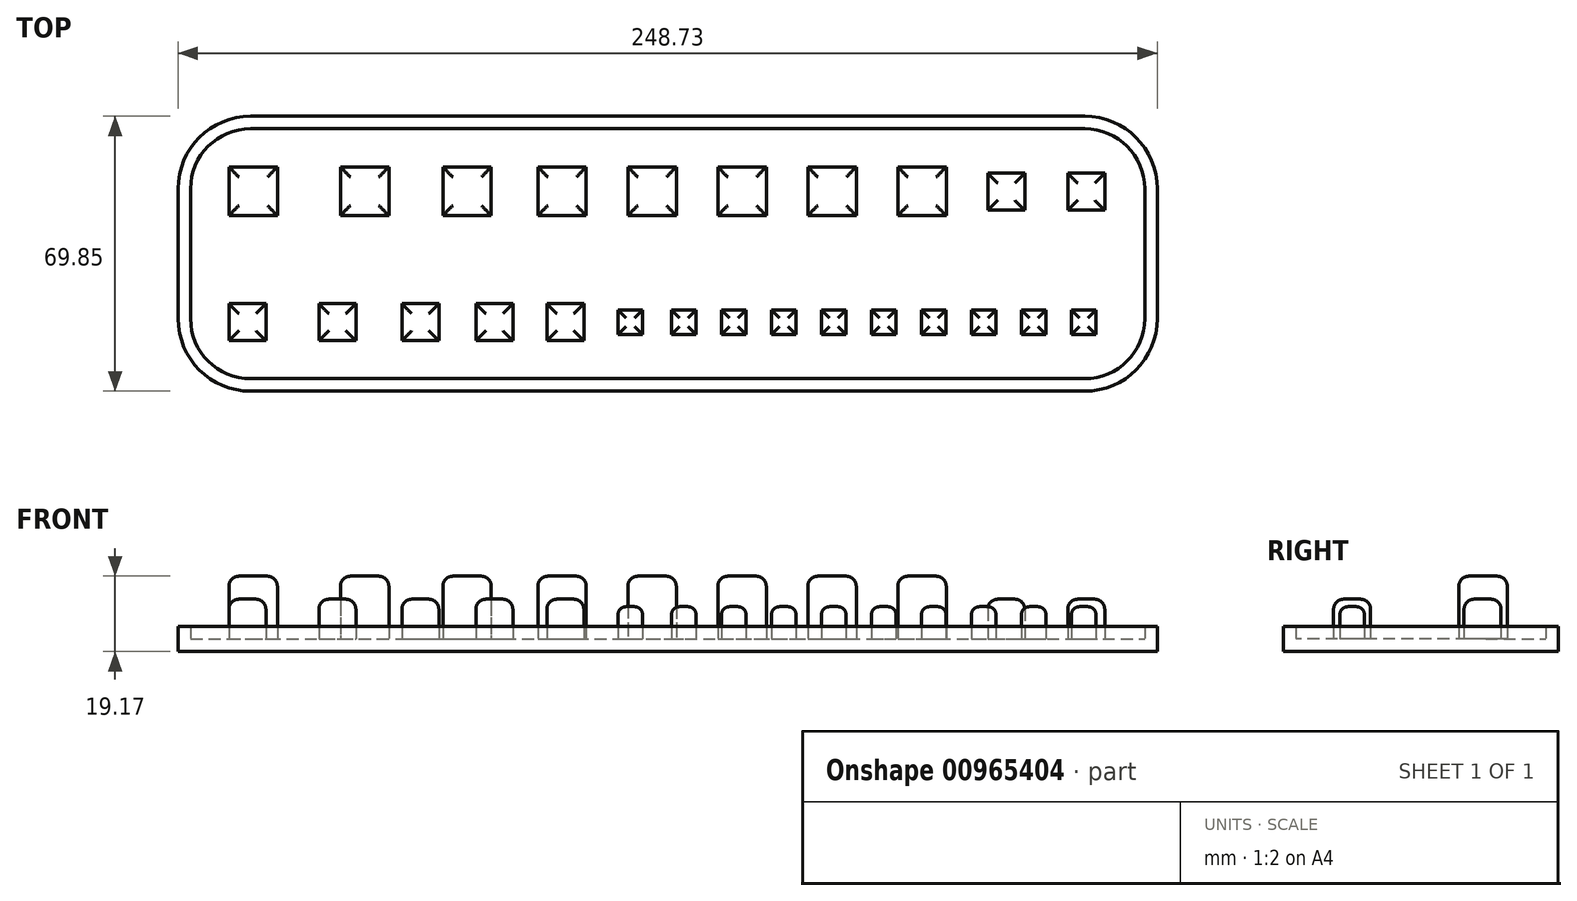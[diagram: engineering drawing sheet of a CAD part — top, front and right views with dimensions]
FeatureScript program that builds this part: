
annotation { "Feature Type Name" : "Feature", "Feature Type Description" : "" }
export const myFeature = defineFeature(function(context is Context, id is Id, definition is map)
    precondition{}
    {
        {
            var Q0;
            Q0=qCreatedBy(makeId("Top.planeOp"),FACE);
            var sketch = newSketch(context, id + "F0", { "sketchPlane" : qUnion([Q0])});
            skLineSegment(sketch, "E0.bottom", {"start": v(-9.72, 9.73) * mm, "end": v(232.66, 9.73) * mm});
            skLineSegment(sketch, "E0.top", {"start": v(-9.72, -53.77) * mm, "end": v(232.66, -53.77) * mm});
            skLineSegment(sketch, "E0.left", {"start": v(-9.72, 9.73) * mm, "end": v(-9.72, -53.77) * mm});
            skLineSegment(sketch, "E0.right", {"start": v(232.66, 9.73) * mm, "end": v(232.66, -53.77) * mm});
            skSolve(sketch);
        }
        {
            var Q0;
            Q0=makeQuery(id+"F0.imprint","IMPRINT",FACE,{"disambiguationData":[TD([[makeQuery(id+"F0.imprint","IMPRINT",EDGE,{"derivedFrom":sQuery(id+"F0.wireOp",EDGE,"E0.bottom")}),-1.0]])]});
            extrude(context, id + "F1", {"entities" : qUnion([Q0]), "oppositeDirection" : true, "depth" : 3.17 * mm, "offsetDistance" : 25.4 * mm});
        }
        {
            var Q0;
            Q0=qCreatedBy(makeId("Top.planeOp"),FACE);
            var sketch = newSketch(context, id + "F2", { "sketchPlane" : qUnion([Q0])});
            skLineSegment(sketch, "E1.bottom", {"start": v(0, 0) * mm, "end": v(12.32, 0) * mm});
            skLineSegment(sketch, "E1.top", {"start": v(0, -12.32) * mm, "end": v(12.32, -12.32) * mm});
            skLineSegment(sketch, "E1.left", {"start": v(0, 0) * mm, "end": v(0, -12.32) * mm});
            skLineSegment(sketch, "E1.right", {"start": v(12.32, 0) * mm, "end": v(12.32, -12.32) * mm});
            skLineSegment(sketch, "E2.1.0.0", {"start": v(28.32, 0) * mm, "end": v(40.64, 0) * mm});
            skLineSegment(sketch, "E2.1.0.1", {"start": v(28.32, -12.32) * mm, "end": v(40.64, -12.32) * mm});
            skLineSegment(sketch, "E2.1.0.2", {"start": v(40.64, 0) * mm, "end": v(40.64, -12.32) * mm});
            skLineSegment(sketch, "E2.1.0.3", {"start": v(28.32, 0) * mm, "end": v(28.32, -12.32) * mm});
            skLineSegment(sketch, "E2.direction1", {"start": v(0, -12.32) * mm, "end": v(28.32, -12.32) * mm, "construction": true});
            skLineSegment(sketch, "E3.1.0.0", {"start": v(54.36, 0) * mm, "end": v(54.36, -12.32) * mm});
            skLineSegment(sketch, "E3.1.0.1", {"start": v(54.36, 0) * mm, "end": v(66.67, 0) * mm});
            skLineSegment(sketch, "E3.1.0.2", {"start": v(54.36, -12.32) * mm, "end": v(66.67, -12.32) * mm});
            skLineSegment(sketch, "E3.1.0.3", {"start": v(66.67, 0) * mm, "end": v(66.67, -12.32) * mm});
            skLineSegment(sketch, "E3.1.0.4", {"start": v(26.04, -12.32) * mm, "end": v(54.36, -12.32) * mm, "construction": true});
            skLineSegment(sketch, "E3.direction1", {"start": v(0, -12.32) * mm, "end": v(26.04, -12.32) * mm, "construction": true});
            skLineSegment(sketch, "E4.1.0.0", {"start": v(78.49, 0) * mm, "end": v(78.49, -12.32) * mm});
            skLineSegment(sketch, "E4.1.0.1", {"start": v(50.16, -12.32) * mm, "end": v(78.49, -12.32) * mm, "construction": true});
            skLineSegment(sketch, "E4.1.0.2", {"start": v(90.8, 0) * mm, "end": v(90.8, -12.32) * mm});
            skLineSegment(sketch, "E4.1.0.3", {"start": v(78.49, -12.32) * mm, "end": v(90.8, -12.32) * mm});
            skLineSegment(sketch, "E4.1.0.4", {"start": v(78.49, 0) * mm, "end": v(90.8, 0) * mm});
            skLineSegment(sketch, "E4.direction1", {"start": v(26.04, -12.32) * mm, "end": v(50.16, -12.32) * mm, "construction": true});
            skLineSegment(sketch, "E5.1.0.0", {"start": v(101.35, 0) * mm, "end": v(101.35, -12.32) * mm});
            skLineSegment(sketch, "E5.1.0.1", {"start": v(113.67, 0) * mm, "end": v(113.67, -12.32) * mm});
            skLineSegment(sketch, "E5.1.0.2", {"start": v(101.35, 0) * mm, "end": v(113.67, 0) * mm});
            skLineSegment(sketch, "E5.1.0.3", {"start": v(101.35, -12.32) * mm, "end": v(113.67, -12.32) * mm});
            skLineSegment(sketch, "E5.1.0.4", {"start": v(73.03, -12.32) * mm, "end": v(101.35, -12.32) * mm, "construction": true});
            skLineSegment(sketch, "E5.direction1", {"start": v(50.16, -12.32) * mm, "end": v(73.03, -12.32) * mm, "construction": true});
            skLineSegment(sketch, "E6.1.0.0", {"start": v(124.2, 0) * mm, "end": v(136.53, 0) * mm});
            skLineSegment(sketch, "E6.1.0.1", {"start": v(124.2, 0) * mm, "end": v(124.2, -12.32) * mm});
            skLineSegment(sketch, "E6.1.0.2", {"start": v(136.53, 0) * mm, "end": v(136.53, -12.32) * mm});
            skLineSegment(sketch, "E6.1.0.3", {"start": v(124.2, -12.32) * mm, "end": v(136.53, -12.32) * mm});
            skLineSegment(sketch, "E6.1.0.4", {"start": v(95.89, -12.32) * mm, "end": v(124.2, -12.32) * mm, "construction": true});
            skLineSegment(sketch, "E6.direction1", {"start": v(72.14, -12.32) * mm, "end": v(95, -12.32) * mm, "construction": true});
            skLineSegment(sketch, "E7.1.0.0", {"start": v(147.07, 0) * mm, "end": v(159.38, 0) * mm});
            skLineSegment(sketch, "E7.1.0.1", {"start": v(159.38, 0) * mm, "end": v(159.38, -12.32) * mm});
            skLineSegment(sketch, "E7.1.0.2", {"start": v(147.07, 0) * mm, "end": v(147.07, -12.32) * mm});
            skLineSegment(sketch, "E7.1.0.3", {"start": v(147.07, -12.32) * mm, "end": v(159.38, -12.32) * mm});
            skLineSegment(sketch, "E7.1.0.4", {"start": v(118.75, -12.32) * mm, "end": v(147.07, -12.32) * mm, "construction": true});
            skLineSegment(sketch, "E7.direction1", {"start": v(95.89, -12.32) * mm, "end": v(118.75, -12.32) * mm, "construction": true});
            skLineSegment(sketch, "E8.1.0.0", {"start": v(141.6, -12.32) * mm, "end": v(169.93, -12.32) * mm, "construction": true});
            skLineSegment(sketch, "E8.1.0.1", {"start": v(169.93, 0) * mm, "end": v(169.93, -12.32) * mm});
            skLineSegment(sketch, "E8.1.0.2", {"start": v(169.93, -12.32) * mm, "end": v(182.25, -12.32) * mm});
            skLineSegment(sketch, "E8.1.0.3", {"start": v(169.93, 0) * mm, "end": v(182.25, 0) * mm});
            skLineSegment(sketch, "E8.1.0.4", {"start": v(182.25, 0) * mm, "end": v(182.25, -12.32) * mm});
            skLineSegment(sketch, "E8.direction1", {"start": v(118.75, -12.32) * mm, "end": v(141.6, -12.32) * mm, "construction": true});
            skSolve(sketch);
        }
        {
            var Q0;
            Q0=makeQuery(id+"F2.imprint","IMPRINT",FACE,{"disambiguationData":[TD([[makeQuery(id+"F2.imprint","IMPRINT",EDGE,{"derivedFrom":sQuery(id+"F2.wireOp",EDGE,"E1.bottom")}),-1.0]])]});
            var Q1;
            Q1=makeQuery(id+"F2.imprint","IMPRINT",FACE,{"disambiguationData":[TD([[makeQuery(id+"F2.imprint","IMPRINT",EDGE,{"derivedFrom":sQuery(id+"F2.wireOp",EDGE,"E2.1.0.0")}),-1.0]])]});
            var Q2;
            Q2=makeQuery(id+"F2.imprint","IMPRINT",FACE,{"disambiguationData":[TD([[makeQuery(id+"F2.imprint","IMPRINT",EDGE,{"derivedFrom":sQuery(id+"F2.wireOp",EDGE,"E3.1.0.0")}),1.0]])]});
            var Q3;
            Q3=makeQuery(id+"F2.imprint","IMPRINT",FACE,{"disambiguationData":[TD([[makeQuery(id+"F2.imprint","IMPRINT",EDGE,{"derivedFrom":sQuery(id+"F2.wireOp",EDGE,"E4.1.0.0")}),1.0]])]});
            var Q4;
            Q4=makeQuery(id+"F2.imprint","IMPRINT",FACE,{"disambiguationData":[TD([[makeQuery(id+"F2.imprint","IMPRINT",EDGE,{"derivedFrom":sQuery(id+"F2.wireOp",EDGE,"E5.1.0.0")}),1.0]])]});
            var Q5;
            Q5=makeQuery(id+"F2.imprint","IMPRINT",FACE,{"disambiguationData":[TD([[makeQuery(id+"F2.imprint","IMPRINT",EDGE,{"derivedFrom":sQuery(id+"F2.wireOp",EDGE,"E6.1.0.0")}),-1.0]])]});
            var Q6;
            Q6=makeQuery(id+"F2.imprint","IMPRINT",FACE,{"disambiguationData":[TD([[makeQuery(id+"F2.imprint","IMPRINT",EDGE,{"derivedFrom":sQuery(id+"F2.wireOp",EDGE,"E7.1.0.0")}),-1.0]])]});
            var Q7;
            Q7=makeQuery(id+"F2.imprint","IMPRINT",FACE,{"disambiguationData":[TD([[makeQuery(id+"F2.imprint","IMPRINT",EDGE,{"derivedFrom":sQuery(id+"F2.wireOp",EDGE,"E8.1.0.1")}),1.0]])]});
            extrude(context, id + "F3", {"entities" : qUnion([Q0, Q1, Q2, Q3, Q4, Q5, Q6, Q7]), "operationType" : NewBodyOperationType.ADD, "depth" : 16 * mm, "offsetDistance" : 25.4 * mm});
        }
        {
            var Q0;
            Q0=makeQuery(id+"F1.opExtrude","CAP_FACE",FACE,{"disambiguationData":[OSD([sQuery(id+"F0.wireOp",EDGE,"E0.bottom"),sQuery(id+"F0.wireOp",EDGE,"E0.top"),sQuery(id+"F0.wireOp",EDGE,"E0.left"),sQuery(id+"F0.wireOp",EDGE,"E0.right")])],"isStart":true});
            var sketch = newSketch(context, id + "F4", { "sketchPlane" : qUnion([Q0])});
            skLineSegment(sketch, "E9", {"start": v(0, -34.73) * mm, "end": v(193.08, -34.73) * mm, "construction": true});
            skLineSegment(sketch, "E10.bottom", {"start": v(0, -34.73) * mm, "end": v(9.4, -34.73) * mm});
            skLineSegment(sketch, "E10.top", {"start": v(0, -44.13) * mm, "end": v(9.4, -44.13) * mm});
            skLineSegment(sketch, "E10.left", {"start": v(0, -34.73) * mm, "end": v(0, -44.13) * mm});
            skLineSegment(sketch, "E10.right", {"start": v(9.4, -34.73) * mm, "end": v(9.4, -44.13) * mm});
            skLineSegment(sketch, "E11.bottom", {"start": v(22.86, -34.73) * mm, "end": v(32.26, -34.73) * mm});
            skLineSegment(sketch, "E11.top", {"start": v(22.86, -44.13) * mm, "end": v(32.26, -44.13) * mm});
            skLineSegment(sketch, "E11.left", {"start": v(22.86, -34.73) * mm, "end": v(22.86, -44.13) * mm});
            skLineSegment(sketch, "E11.right", {"start": v(32.26, -34.73) * mm, "end": v(32.26, -44.13) * mm});
            skLineSegment(sketch, "E12.bottom", {"start": v(43.94, -34.73) * mm, "end": v(53.34, -34.73) * mm});
            skLineSegment(sketch, "E12.top", {"start": v(43.94, -44.13) * mm, "end": v(53.34, -44.13) * mm});
            skLineSegment(sketch, "E12.left", {"start": v(43.94, -34.73) * mm, "end": v(43.94, -44.13) * mm});
            skLineSegment(sketch, "E12.right", {"start": v(53.34, -34.73) * mm, "end": v(53.34, -44.13) * mm});
            skLineSegment(sketch, "E13.bottom", {"start": v(62.74, -34.73) * mm, "end": v(72.14, -34.73) * mm});
            skLineSegment(sketch, "E13.top", {"start": v(62.74, -44.13) * mm, "end": v(72.14, -44.13) * mm});
            skLineSegment(sketch, "E13.left", {"start": v(62.74, -34.73) * mm, "end": v(62.74, -44.13) * mm});
            skLineSegment(sketch, "E13.right", {"start": v(72.14, -34.73) * mm, "end": v(72.14, -44.13) * mm});
            skLineSegment(sketch, "E14.bottom", {"start": v(80.77, -34.73) * mm, "end": v(90.17, -34.73) * mm});
            skLineSegment(sketch, "E14.top", {"start": v(80.77, -44.13) * mm, "end": v(90.17, -44.13) * mm});
            skLineSegment(sketch, "E14.left", {"start": v(80.77, -34.73) * mm, "end": v(80.77, -44.13) * mm});
            skLineSegment(sketch, "E14.right", {"start": v(90.17, -34.73) * mm, "end": v(90.17, -44.13) * mm});
            skLineSegment(sketch, "E15.bottom", {"start": v(192.79, -1.59) * mm, "end": v(202.18, -1.59) * mm});
            skLineSegment(sketch, "E15.top", {"start": v(192.79, -10.99) * mm, "end": v(202.18, -10.99) * mm});
            skLineSegment(sketch, "E15.left", {"start": v(192.79, -1.59) * mm, "end": v(192.79, -10.99) * mm});
            skLineSegment(sketch, "E15.right", {"start": v(202.18, -1.59) * mm, "end": v(202.18, -10.99) * mm});
            skLineSegment(sketch, "E16.1.0.0", {"start": v(213.1, -1.59) * mm, "end": v(222.5, -1.59) * mm});
            skLineSegment(sketch, "E16.1.0.1", {"start": v(213.1, -10.99) * mm, "end": v(222.5, -10.99) * mm});
            skLineSegment(sketch, "E16.1.0.2", {"start": v(222.5, -1.59) * mm, "end": v(222.5, -10.99) * mm});
            skLineSegment(sketch, "E16.1.0.3", {"start": v(213.1, -1.59) * mm, "end": v(213.1, -10.99) * mm});
            skLineSegment(sketch, "E16.direction1", {"start": v(192.79, -10.99) * mm, "end": v(213.1, -10.99) * mm, "construction": true});
            skSolve(sketch);
        }
        {
            var Q0;
            Q0=makeQuery(id+"F4.imprint","IMPRINT",FACE,{"disambiguationData":[TD([[makeQuery(id+"F4.imprint","IMPRINT",EDGE,{"derivedFrom":sQuery(id+"F4.wireOp",EDGE,"E12.bottom")}),-1.0]])]});
            var Q1;
            Q1=makeQuery(id+"F4.imprint","IMPRINT",FACE,{"disambiguationData":[TD([[makeQuery(id+"F4.imprint","IMPRINT",EDGE,{"derivedFrom":sQuery(id+"F4.wireOp",EDGE,"E13.bottom")}),-1.0]])]});
            var Q2;
            Q2=makeQuery(id+"F4.imprint","IMPRINT",FACE,{"disambiguationData":[TD([[makeQuery(id+"F4.imprint","IMPRINT",EDGE,{"derivedFrom":sQuery(id+"F4.wireOp",EDGE,"E14.bottom")}),-1.0]])]});
            var Q3;
            Q3=makeQuery(id+"F4.imprint","IMPRINT",FACE,{"disambiguationData":[TD([[makeQuery(id+"F4.imprint","IMPRINT",EDGE,{"derivedFrom":sQuery(id+"F4.wireOp",EDGE,"HuPphu0x-Gtiq-LhBo-5UTa-TvdvrvVJAFvw.bottom")}),-1.0]])]});
            var Q4;
            Q4=makeQuery(id+"F4.imprint","IMPRINT",FACE,{"disambiguationData":[TD([[makeQuery(id+"F4.imprint","IMPRINT",EDGE,{"derivedFrom":sQuery(id+"F4.wireOp",EDGE,"E11.bottom")}),-1.0]])]});
            var Q5;
            Q5=makeQuery(id+"F4.imprint","IMPRINT",FACE,{"disambiguationData":[TD([[makeQuery(id+"F4.imprint","IMPRINT",EDGE,{"derivedFrom":sQuery(id+"F4.wireOp",EDGE,"E10.bottom")}),-1.0]])]});
            var Q6;
            Q6=makeQuery(id+"F4.imprint","IMPRINT",FACE,{"disambiguationData":[TD([[makeQuery(id+"F4.imprint","IMPRINT",EDGE,{"derivedFrom":sQuery(id+"F4.wireOp",EDGE,"E15.bottom")}),-1.0]])]});
            var Q7;
            Q7=makeQuery(id+"F4.imprint","IMPRINT",FACE,{"disambiguationData":[TD([[makeQuery(id+"F4.imprint","IMPRINT",EDGE,{"derivedFrom":sQuery(id+"F4.wireOp",EDGE,"E16.1.0.0")}),-1.0]])]});
            extrude(context, id + "F5", {"entities" : qUnion([Q0, Q1, Q2, Q3, Q4, Q5, Q6, Q7]), "operationType" : NewBodyOperationType.ADD, "depth" : 10.16 * mm, "offsetDistance" : 25.4 * mm});
        }
        {
            var Q0;
            Q0=makeQuery(id+"F1.opExtrude","SWEPT_EDGE",EDGE,{"disambiguationData":[OSD([sQuery(id+"F0.wireOp",EDGE,"E0.bottom"),sQuery(id+"F0.wireOp",EDGE,"E0.left")])]});
            var Q1;
            Q1=makeQuery(id+"F1.opExtrude","SWEPT_EDGE",EDGE,{"disambiguationData":[OSD([sQuery(id+"F0.wireOp",EDGE,"E0.bottom"),sQuery(id+"F0.wireOp",EDGE,"E0.right")])]});
            var Q2;
            Q2=makeQuery(id+"F1.opExtrude","SWEPT_EDGE",EDGE,{"disambiguationData":[OSD([sQuery(id+"F0.wireOp",EDGE,"E0.top"),sQuery(id+"F0.wireOp",EDGE,"E0.right")])]});
            var Q3;
            Q3=makeQuery(id+"F1.opExtrude","SWEPT_EDGE",EDGE,{"disambiguationData":[OSD([sQuery(id+"F0.wireOp",EDGE,"E0.top"),sQuery(id+"F0.wireOp",EDGE,"E0.left")])]});
            fillet(context, id + "F6", {"entities" : qUnion([Q0, Q1, Q2, Q3]), "radius" : 15.24 * mm, "tangentPropagation" : true, "allowEdgeOverflow" : false});
        }
        {
            var Q0;
            Q0=makeQuery(id+"F3.opExtrude","CAP_FACE",FACE,{"disambiguationData":[OSD([sQuery(id+"F2.wireOp",EDGE,"E1.bottom"),sQuery(id+"F2.wireOp",EDGE,"E1.top"),sQuery(id+"F2.wireOp",EDGE,"E1.left"),sQuery(id+"F2.wireOp",EDGE,"E1.right")])],"isStart":false});
            var Q1;
            Q1=makeQuery(id+"F3.opExtrude","CAP_FACE",FACE,{"disambiguationData":[OSD([sQuery(id+"F2.wireOp",EDGE,"E2.1.0.0"),sQuery(id+"F2.wireOp",EDGE,"E2.1.0.1"),sQuery(id+"F2.wireOp",EDGE,"E2.1.0.2"),sQuery(id+"F2.wireOp",EDGE,"E2.1.0.3")])],"isStart":false});
            var Q2;
            Q2=makeQuery(id+"F3.opExtrude","CAP_FACE",FACE,{"disambiguationData":[OSD([sQuery(id+"F2.wireOp",EDGE,"E3.1.0.0"),sQuery(id+"F2.wireOp",EDGE,"E3.1.0.1"),sQuery(id+"F2.wireOp",EDGE,"E3.1.0.2"),sQuery(id+"F2.wireOp",EDGE,"E3.1.0.3")])],"isStart":false});
            var Q3;
            Q3=makeQuery(id+"F3.opExtrude","CAP_FACE",FACE,{"disambiguationData":[OSD([sQuery(id+"F2.wireOp",EDGE,"E4.1.0.0"),sQuery(id+"F2.wireOp",EDGE,"E4.1.0.2"),sQuery(id+"F2.wireOp",EDGE,"E4.1.0.3"),sQuery(id+"F2.wireOp",EDGE,"E4.1.0.4")])],"isStart":false});
            var Q4;
            Q4=makeQuery(id+"F3.opExtrude","CAP_FACE",FACE,{"disambiguationData":[OSD([sQuery(id+"F2.wireOp",EDGE,"E5.1.0.0"),sQuery(id+"F2.wireOp",EDGE,"E5.1.0.1"),sQuery(id+"F2.wireOp",EDGE,"E5.1.0.2"),sQuery(id+"F2.wireOp",EDGE,"E5.1.0.3")])],"isStart":false});
            var Q5;
            Q5=makeQuery(id+"F3.opExtrude","CAP_FACE",FACE,{"disambiguationData":[OSD([sQuery(id+"F2.wireOp",EDGE,"E6.1.0.0"),sQuery(id+"F2.wireOp",EDGE,"E6.1.0.1"),sQuery(id+"F2.wireOp",EDGE,"E6.1.0.2"),sQuery(id+"F2.wireOp",EDGE,"E6.1.0.3")])],"isStart":false});
            var Q6;
            Q6=makeQuery(id+"F3.opExtrude","CAP_FACE",FACE,{"disambiguationData":[OSD([sQuery(id+"F2.wireOp",EDGE,"E7.1.0.0"),sQuery(id+"F2.wireOp",EDGE,"E7.1.0.1"),sQuery(id+"F2.wireOp",EDGE,"E7.1.0.2"),sQuery(id+"F2.wireOp",EDGE,"E7.1.0.3")])],"isStart":false});
            var Q7;
            Q7=makeQuery(id+"F3.opExtrude","CAP_FACE",FACE,{"disambiguationData":[OSD([sQuery(id+"F2.wireOp",EDGE,"E8.1.0.1"),sQuery(id+"F2.wireOp",EDGE,"E8.1.0.2"),sQuery(id+"F2.wireOp",EDGE,"E8.1.0.3"),sQuery(id+"F2.wireOp",EDGE,"E8.1.0.4")])],"isStart":false});
            fillet(context, id + "F7", {"entities" : qUnion([Q0, Q1, Q2, Q3, Q4, Q5, Q6, Q7]), "radius" : 2.54 * mm, "tangentPropagation" : true, "allowEdgeOverflow" : false});
        }
        {
            var Q0;
            Q0=makeQuery(id+"F5.opExtrude","CAP_FACE",FACE,{"disambiguationData":[OSD([sQuery(id+"F4.wireOp",EDGE,"E10.bottom"),sQuery(id+"F4.wireOp",EDGE,"E10.top"),sQuery(id+"F4.wireOp",EDGE,"E10.left"),sQuery(id+"F4.wireOp",EDGE,"E10.right")])],"isStart":false});
            var Q1;
            Q1=makeQuery(id+"F5.opExtrude","CAP_FACE",FACE,{"disambiguationData":[OSD([sQuery(id+"F4.wireOp",EDGE,"E11.bottom"),sQuery(id+"F4.wireOp",EDGE,"E11.top"),sQuery(id+"F4.wireOp",EDGE,"E11.left"),sQuery(id+"F4.wireOp",EDGE,"E11.right")])],"isStart":false});
            var Q2;
            Q2=makeQuery(id+"F5.opExtrude","CAP_FACE",FACE,{"disambiguationData":[OSD([sQuery(id+"F4.wireOp",EDGE,"E12.bottom"),sQuery(id+"F4.wireOp",EDGE,"E12.top"),sQuery(id+"F4.wireOp",EDGE,"E12.left"),sQuery(id+"F4.wireOp",EDGE,"E12.right")])],"isStart":false});
            var Q3;
            Q3=makeQuery(id+"F5.opExtrude","CAP_FACE",FACE,{"disambiguationData":[OSD([sQuery(id+"F4.wireOp",EDGE,"E13.bottom"),sQuery(id+"F4.wireOp",EDGE,"E13.top"),sQuery(id+"F4.wireOp",EDGE,"E13.left"),sQuery(id+"F4.wireOp",EDGE,"E13.right")])],"isStart":false});
            var Q4;
            Q4=makeQuery(id+"F5.opExtrude","CAP_FACE",FACE,{"disambiguationData":[OSD([sQuery(id+"F4.wireOp",EDGE,"E14.bottom"),sQuery(id+"F4.wireOp",EDGE,"E14.top"),sQuery(id+"F4.wireOp",EDGE,"E14.left"),sQuery(id+"F4.wireOp",EDGE,"E14.right")])],"isStart":false});
            var Q5;
            Q5=makeQuery(id+"F5.opExtrude","CAP_FACE",FACE,{"disambiguationData":[OSD([sQuery(id+"F4.wireOp",EDGE,"HuPphu0x-Gtiq-LhBo-5UTa-TvdvrvVJAFvw.bottom"),sQuery(id+"F4.wireOp",EDGE,"HuPphu0x-Gtiq-LhBo-5UTa-TvdvrvVJAFvw.top"),sQuery(id+"F4.wireOp",EDGE,"HuPphu0x-Gtiq-LhBo-5UTa-TvdvrvVJAFvw.left"),sQuery(id+"F4.wireOp",EDGE,"HuPphu0x-Gtiq-LhBo-5UTa-TvdvrvVJAFvw.right")])],"isStart":false});
            var Q6;
            Q6=makeQuery(id+"F5.opExtrude","CAP_FACE",FACE,{"disambiguationData":[OSD([sQuery(id+"F4.wireOp",EDGE,"E15.bottom"),sQuery(id+"F4.wireOp",EDGE,"E15.top"),sQuery(id+"F4.wireOp",EDGE,"E15.left"),sQuery(id+"F4.wireOp",EDGE,"E15.right")])],"isStart":false});
            var Q7;
            Q7=makeQuery(id+"F5.opExtrude","CAP_FACE",FACE,{"disambiguationData":[OSD([sQuery(id+"F4.wireOp",EDGE,"E16.1.0.0"),sQuery(id+"F4.wireOp",EDGE,"E16.1.0.1"),sQuery(id+"F4.wireOp",EDGE,"E16.1.0.2"),sQuery(id+"F4.wireOp",EDGE,"E16.1.0.3")])],"isStart":false});
            fillet(context, id + "F8", {"entities" : qUnion([Q0, Q1, Q2, Q3, Q4, Q5, Q6, Q7]), "radius" : 2.54 * mm, "tangentPropagation" : true, "allowEdgeOverflow" : false});
        }
        {
            var Q0;
            Q0=makeQuery(id+"F1.opExtrude","CAP_FACE",FACE,{"disambiguationData":[OSD([sQuery(id+"F0.wireOp",EDGE,"E0.bottom"),sQuery(id+"F0.wireOp",EDGE,"E0.top"),sQuery(id+"F0.wireOp",EDGE,"E0.left"),sQuery(id+"F0.wireOp",EDGE,"E0.right")])],"isStart":true});
            var sketch = newSketch(context, id + "F9", { "sketchPlane" : qUnion([Q0])});
            skLineSegment(sketch, "E17", {"start": v(113.95, -36.32) * mm, "end": v(235.74, -36.32) * mm, "construction": true});
            skLineSegment(sketch, "E18.bottom", {"start": v(98.87, -36.32) * mm, "end": v(105.1, -36.32) * mm});
            skLineSegment(sketch, "E18.top", {"start": v(98.87, -42.55) * mm, "end": v(105.1, -42.55) * mm});
            skLineSegment(sketch, "E18.left", {"start": v(98.87, -36.32) * mm, "end": v(98.87, -42.55) * mm});
            skLineSegment(sketch, "E18.right", {"start": v(105.1, -36.32) * mm, "end": v(105.1, -42.55) * mm});
            skPoint(sketch, "E19.oppositeSnap0", {"position": v(101.98, -42.55) * mm});
            skLineSegment(sketch, "E19.bottom", {"start": v(112.46, -36.32) * mm, "end": v(118.68, -36.32) * mm});
            skLineSegment(sketch, "E19.top", {"start": v(112.46, -42.55) * mm, "end": v(118.68, -42.55) * mm});
            skLineSegment(sketch, "E19.left", {"start": v(112.46, -36.32) * mm, "end": v(112.46, -42.54) * mm});
            skLineSegment(sketch, "E19.right", {"start": v(118.68, -36.32) * mm, "end": v(118.68, -42.54) * mm});
            skLineSegment(sketch, "E20.1.0.0", {"start": v(125.16, -36.32) * mm, "end": v(125.16, -42.54) * mm});
            skLineSegment(sketch, "E20.1.0.1", {"start": v(125.16, -42.55) * mm, "end": v(131.38, -42.55) * mm});
            skLineSegment(sketch, "E20.1.0.2", {"start": v(131.38, -36.32) * mm, "end": v(131.38, -42.54) * mm});
            skLineSegment(sketch, "E20.1.0.3", {"start": v(125.16, -36.32) * mm, "end": v(131.38, -36.32) * mm});
            skLineSegment(sketch, "E20.2.0.0", {"start": v(137.86, -36.32) * mm, "end": v(137.86, -42.54) * mm});
            skLineSegment(sketch, "E20.2.0.1", {"start": v(137.86, -42.55) * mm, "end": v(144.08, -42.55) * mm});
            skLineSegment(sketch, "E20.2.0.2", {"start": v(144.08, -36.32) * mm, "end": v(144.08, -42.54) * mm});
            skLineSegment(sketch, "E20.2.0.3", {"start": v(137.86, -36.32) * mm, "end": v(144.08, -36.32) * mm});
            skLineSegment(sketch, "E20.3.0.0", {"start": v(150.56, -36.32) * mm, "end": v(150.56, -42.54) * mm});
            skLineSegment(sketch, "E20.3.0.1", {"start": v(150.56, -42.55) * mm, "end": v(156.78, -42.55) * mm});
            skLineSegment(sketch, "E20.3.0.2", {"start": v(156.78, -36.32) * mm, "end": v(156.78, -42.54) * mm});
            skLineSegment(sketch, "E20.3.0.3", {"start": v(150.56, -36.32) * mm, "end": v(156.78, -36.32) * mm});
            skLineSegment(sketch, "E20.4.0.0", {"start": v(163.26, -36.32) * mm, "end": v(163.26, -42.54) * mm});
            skLineSegment(sketch, "E20.4.0.1", {"start": v(163.26, -42.55) * mm, "end": v(169.48, -42.55) * mm});
            skLineSegment(sketch, "E20.4.0.2", {"start": v(169.48, -36.32) * mm, "end": v(169.48, -42.54) * mm});
            skLineSegment(sketch, "E20.4.0.3", {"start": v(163.26, -36.32) * mm, "end": v(169.48, -36.32) * mm});
            skLineSegment(sketch, "E20.5.0.0", {"start": v(175.96, -36.32) * mm, "end": v(175.96, -42.54) * mm});
            skLineSegment(sketch, "E20.5.0.1", {"start": v(175.96, -42.55) * mm, "end": v(182.18, -42.55) * mm});
            skLineSegment(sketch, "E20.5.0.2", {"start": v(182.18, -36.32) * mm, "end": v(182.18, -42.54) * mm});
            skLineSegment(sketch, "E20.5.0.3", {"start": v(175.96, -36.32) * mm, "end": v(182.18, -36.32) * mm});
            skLineSegment(sketch, "E20.6.0.0", {"start": v(188.66, -36.32) * mm, "end": v(188.66, -42.54) * mm});
            skLineSegment(sketch, "E20.6.0.1", {"start": v(188.66, -42.55) * mm, "end": v(194.88, -42.55) * mm});
            skLineSegment(sketch, "E20.6.0.2", {"start": v(194.88, -36.32) * mm, "end": v(194.88, -42.54) * mm});
            skLineSegment(sketch, "E20.6.0.3", {"start": v(188.66, -36.32) * mm, "end": v(194.88, -36.32) * mm});
            skLineSegment(sketch, "E20.7.0.0", {"start": v(201.36, -36.32) * mm, "end": v(201.36, -42.54) * mm});
            skLineSegment(sketch, "E20.7.0.1", {"start": v(201.36, -42.55) * mm, "end": v(207.58, -42.55) * mm});
            skLineSegment(sketch, "E20.7.0.2", {"start": v(207.58, -36.32) * mm, "end": v(207.58, -42.54) * mm});
            skLineSegment(sketch, "E20.7.0.3", {"start": v(201.36, -36.32) * mm, "end": v(207.58, -36.32) * mm});
            skLineSegment(sketch, "E20.8.0.0", {"start": v(214.06, -36.32) * mm, "end": v(214.06, -42.54) * mm});
            skLineSegment(sketch, "E20.8.0.1", {"start": v(214.06, -42.55) * mm, "end": v(220.28, -42.55) * mm});
            skLineSegment(sketch, "E20.8.0.2", {"start": v(220.28, -36.32) * mm, "end": v(220.28, -42.54) * mm});
            skLineSegment(sketch, "E20.8.0.3", {"start": v(214.06, -36.32) * mm, "end": v(220.28, -36.32) * mm});
            skLineSegment(sketch, "E20.direction1", {"start": v(112.46, -42.55) * mm, "end": v(125.16, -42.55) * mm, "construction": true});
            skSolve(sketch);
        }
        {
            var Q0;
            Q0=makeQuery(id+"F9.imprint","IMPRINT",FACE,{"disambiguationData":[TD([[makeQuery(id+"F9.imprint","IMPRINT",EDGE,{"derivedFrom":sQuery(id+"F9.wireOp",EDGE,"E18.bottom")}),-1.0]])]});
            var Q1;
            Q1=makeQuery(id+"F9.imprint","IMPRINT",FACE,{"disambiguationData":[TD([[makeQuery(id+"F9.imprint","IMPRINT",EDGE,{"derivedFrom":sQuery(id+"F9.wireOp",EDGE,"E19.bottom")}),-1.0]])]});
            var Q2;
            Q2=makeQuery(id+"F9.imprint","IMPRINT",FACE,{"disambiguationData":[TD([[makeQuery(id+"F9.imprint","IMPRINT",EDGE,{"derivedFrom":sQuery(id+"F9.wireOp",EDGE,"E20.1.0.0")}),1.0]])]});
            var Q3;
            Q3=makeQuery(id+"F9.imprint","IMPRINT",FACE,{"disambiguationData":[TD([[makeQuery(id+"F9.imprint","IMPRINT",EDGE,{"derivedFrom":sQuery(id+"F9.wireOp",EDGE,"E20.2.0.0")}),1.0]])]});
            var Q4;
            Q4=makeQuery(id+"F9.imprint","IMPRINT",FACE,{"disambiguationData":[TD([[makeQuery(id+"F9.imprint","IMPRINT",EDGE,{"derivedFrom":sQuery(id+"F9.wireOp",EDGE,"E20.3.0.0")}),1.0]])]});
            var Q5;
            Q5=makeQuery(id+"F9.imprint","IMPRINT",FACE,{"disambiguationData":[TD([[makeQuery(id+"F9.imprint","IMPRINT",EDGE,{"derivedFrom":sQuery(id+"F9.wireOp",EDGE,"E20.4.0.0")}),1.0]])]});
            var Q6;
            Q6=makeQuery(id+"F9.imprint","IMPRINT",FACE,{"disambiguationData":[TD([[makeQuery(id+"F9.imprint","IMPRINT",EDGE,{"derivedFrom":sQuery(id+"F9.wireOp",EDGE,"E20.5.0.0")}),1.0]])]});
            var Q7;
            Q7=makeQuery(id+"F9.imprint","IMPRINT",FACE,{"disambiguationData":[TD([[makeQuery(id+"F9.imprint","IMPRINT",EDGE,{"derivedFrom":sQuery(id+"F9.wireOp",EDGE,"E20.6.0.0")}),1.0]])]});
            var Q8;
            Q8=makeQuery(id+"F9.imprint","IMPRINT",FACE,{"disambiguationData":[TD([[makeQuery(id+"F9.imprint","IMPRINT",EDGE,{"derivedFrom":sQuery(id+"F9.wireOp",EDGE,"E20.7.0.0")}),1.0]])]});
            var Q9;
            Q9=makeQuery(id+"F9.imprint","IMPRINT",FACE,{"disambiguationData":[TD([[makeQuery(id+"F9.imprint","IMPRINT",EDGE,{"derivedFrom":sQuery(id+"F9.wireOp",EDGE,"E20.8.0.0")}),1.0]])]});
            var Q10;
            Q10=sQuery(id+"F9.wireOp",EDGE,"E18.left");
            var Q11;
            Q11=sQuery(id+"F9.wireOp",EDGE,"E18.bottom");
            var Q12;
            Q12=sQuery(id+"F9.wireOp",EDGE,"E18.right");
            var Q13;
            Q13=sQuery(id+"F9.wireOp",EDGE,"E18.top");
            extrude(context, id + "F10", {"entities" : qUnion([Q0, Q1, Q2, Q3, Q4, Q5, Q6, Q7, Q8, Q9]), "operationType" : NewBodyOperationType.ADD, "surfaceEntities" : qUnion([Q10, Q11, Q12, Q13]), "depth" : 8.25 * mm, "offsetDistance" : 25.4 * mm});
        }
        {
            var Q0;
            Q0=makeQuery(id+"F10.opExtrude","CAP_FACE",FACE,{"disambiguationData":[OSD([sQuery(id+"F9.wireOp",EDGE,"E18.bottom"),sQuery(id+"F9.wireOp",EDGE,"E18.top"),sQuery(id+"F9.wireOp",EDGE,"E18.left"),sQuery(id+"F9.wireOp",EDGE,"E18.right")])],"isStart":false});
            var Q1;
            Q1=makeQuery(id+"F10.opExtrude","CAP_FACE",FACE,{"disambiguationData":[OSD([sQuery(id+"F9.wireOp",EDGE,"E19.bottom"),sQuery(id+"F9.wireOp",EDGE,"E19.top"),sQuery(id+"F9.wireOp",EDGE,"E19.left"),sQuery(id+"F9.wireOp",EDGE,"E19.right")])],"isStart":false});
            var Q2;
            Q2=makeQuery(id+"F10.opExtrude","CAP_FACE",FACE,{"disambiguationData":[OSD([sQuery(id+"F9.wireOp",EDGE,"E20.1.0.0"),sQuery(id+"F9.wireOp",EDGE,"E20.1.0.1"),sQuery(id+"F9.wireOp",EDGE,"E20.1.0.2"),sQuery(id+"F9.wireOp",EDGE,"E20.1.0.3")])],"isStart":false});
            var Q3;
            Q3=makeQuery(id+"F10.opExtrude","CAP_FACE",FACE,{"disambiguationData":[OSD([sQuery(id+"F9.wireOp",EDGE,"E20.2.0.0"),sQuery(id+"F9.wireOp",EDGE,"E20.2.0.1"),sQuery(id+"F9.wireOp",EDGE,"E20.2.0.2"),sQuery(id+"F9.wireOp",EDGE,"E20.2.0.3")])],"isStart":false});
            var Q4;
            Q4=makeQuery(id+"F10.opExtrude","CAP_FACE",FACE,{"disambiguationData":[OSD([sQuery(id+"F9.wireOp",EDGE,"E20.3.0.0"),sQuery(id+"F9.wireOp",EDGE,"E20.3.0.1"),sQuery(id+"F9.wireOp",EDGE,"E20.3.0.2"),sQuery(id+"F9.wireOp",EDGE,"E20.3.0.3")])],"isStart":false});
            var Q5;
            Q5=makeQuery(id+"F10.opExtrude","CAP_FACE",FACE,{"disambiguationData":[OSD([sQuery(id+"F9.wireOp",EDGE,"E20.4.0.0"),sQuery(id+"F9.wireOp",EDGE,"E20.4.0.1"),sQuery(id+"F9.wireOp",EDGE,"E20.4.0.2"),sQuery(id+"F9.wireOp",EDGE,"E20.4.0.3")])],"isStart":false});
            var Q6;
            Q6=makeQuery(id+"F10.opExtrude","CAP_FACE",FACE,{"disambiguationData":[OSD([sQuery(id+"F9.wireOp",EDGE,"E20.5.0.0"),sQuery(id+"F9.wireOp",EDGE,"E20.5.0.1"),sQuery(id+"F9.wireOp",EDGE,"E20.5.0.2"),sQuery(id+"F9.wireOp",EDGE,"E20.5.0.3")])],"isStart":false});
            var Q7;
            Q7=makeQuery(id+"F10.opExtrude","CAP_FACE",FACE,{"disambiguationData":[OSD([sQuery(id+"F9.wireOp",EDGE,"E20.6.0.0"),sQuery(id+"F9.wireOp",EDGE,"E20.6.0.1"),sQuery(id+"F9.wireOp",EDGE,"E20.6.0.2"),sQuery(id+"F9.wireOp",EDGE,"E20.6.0.3")])],"isStart":false});
            var Q8;
            Q8=makeQuery(id+"F10.opExtrude","CAP_FACE",FACE,{"disambiguationData":[OSD([sQuery(id+"F9.wireOp",EDGE,"E20.7.0.0"),sQuery(id+"F9.wireOp",EDGE,"E20.7.0.1"),sQuery(id+"F9.wireOp",EDGE,"E20.7.0.2"),sQuery(id+"F9.wireOp",EDGE,"E20.7.0.3")])],"isStart":false});
            var Q9;
            Q9=makeQuery(id+"F10.opExtrude","CAP_FACE",FACE,{"disambiguationData":[OSD([sQuery(id+"F9.wireOp",EDGE,"E20.8.0.0"),sQuery(id+"F9.wireOp",EDGE,"E20.8.0.1"),sQuery(id+"F9.wireOp",EDGE,"E20.8.0.2"),sQuery(id+"F9.wireOp",EDGE,"E20.8.0.3")])],"isStart":false});
            fillet(context, id + "F11", {"entities" : qUnion([Q0, Q1, Q2, Q3, Q4, Q5, Q6, Q7, Q8, Q9]), "radius" : 2.03 * mm, "tangentPropagation" : true, "allowEdgeOverflow" : false});
        }
        {
            var Q0;
            Q0=makeQuery(id+"F1.opExtrude","CAP_FACE",FACE,{"disambiguationData":[OSD([sQuery(id+"F0.wireOp",EDGE,"E0.bottom"),sQuery(id+"F0.wireOp",EDGE,"E0.top"),sQuery(id+"F0.wireOp",EDGE,"E0.left"),sQuery(id+"F0.wireOp",EDGE,"E0.right")])],"isStart":false});
            var sketch = newSketch(context, id + "F12", { "sketchPlane" : qUnion([Q0])});
            skArc(sketch, "E21.0", {"start": v(5.52, 56.95) * mm, "mid": v(-7.5, 51.55) * mm, "end": v(-12.9, 38.53) * mm});
            skLineSegment(sketch, "E21.1", {"start": v(-12.9, 5.51) * mm, "end": v(-12.9, 38.53) * mm});
            skLineSegment(sketch, "E21.2", {"start": v(5.52, 56.95) * mm, "end": v(217.42, 56.95) * mm});
            skArc(sketch, "E21.3", {"start": v(-12.9, 5.51) * mm, "mid": v(-7.5, -7.5) * mm, "end": v(5.52, -12.9) * mm});
            skArc(sketch, "E21.4", {"start": v(235.84, 38.53) * mm, "mid": v(230.45, 51.55) * mm, "end": v(217.42, 56.95) * mm});
            skLineSegment(sketch, "E21.5", {"start": v(235.84, 5.51) * mm, "end": v(235.84, 38.53) * mm});
            skArc(sketch, "E21.6", {"start": v(217.42, -12.9) * mm, "mid": v(230.45, -7.5) * mm, "end": v(235.84, 5.51) * mm});
            skLineSegment(sketch, "E21.7", {"start": v(5.52, -12.9) * mm, "end": v(217.42, -12.9) * mm});
            skSolve(sketch);
        }
        {
            var Q0;
            Q0=makeQuery(id+"F12.imprint","IMPRINT",FACE,{"disambiguationData":[TD([[makeQuery(id+"F12.imprint","IMPRINT",EDGE,{"derivedFrom":sQuery(id+"F12.wireOp",EDGE,"E21.0")}),1.0]])]});
            extrude(context, id + "F13", {"entities" : qUnion([Q0]), "operationType" : NewBodyOperationType.ADD, "oppositeDirection" : true, "depth" : 6.35 * mm, "offsetDistance" : 25.4 * mm});
        }
    });
